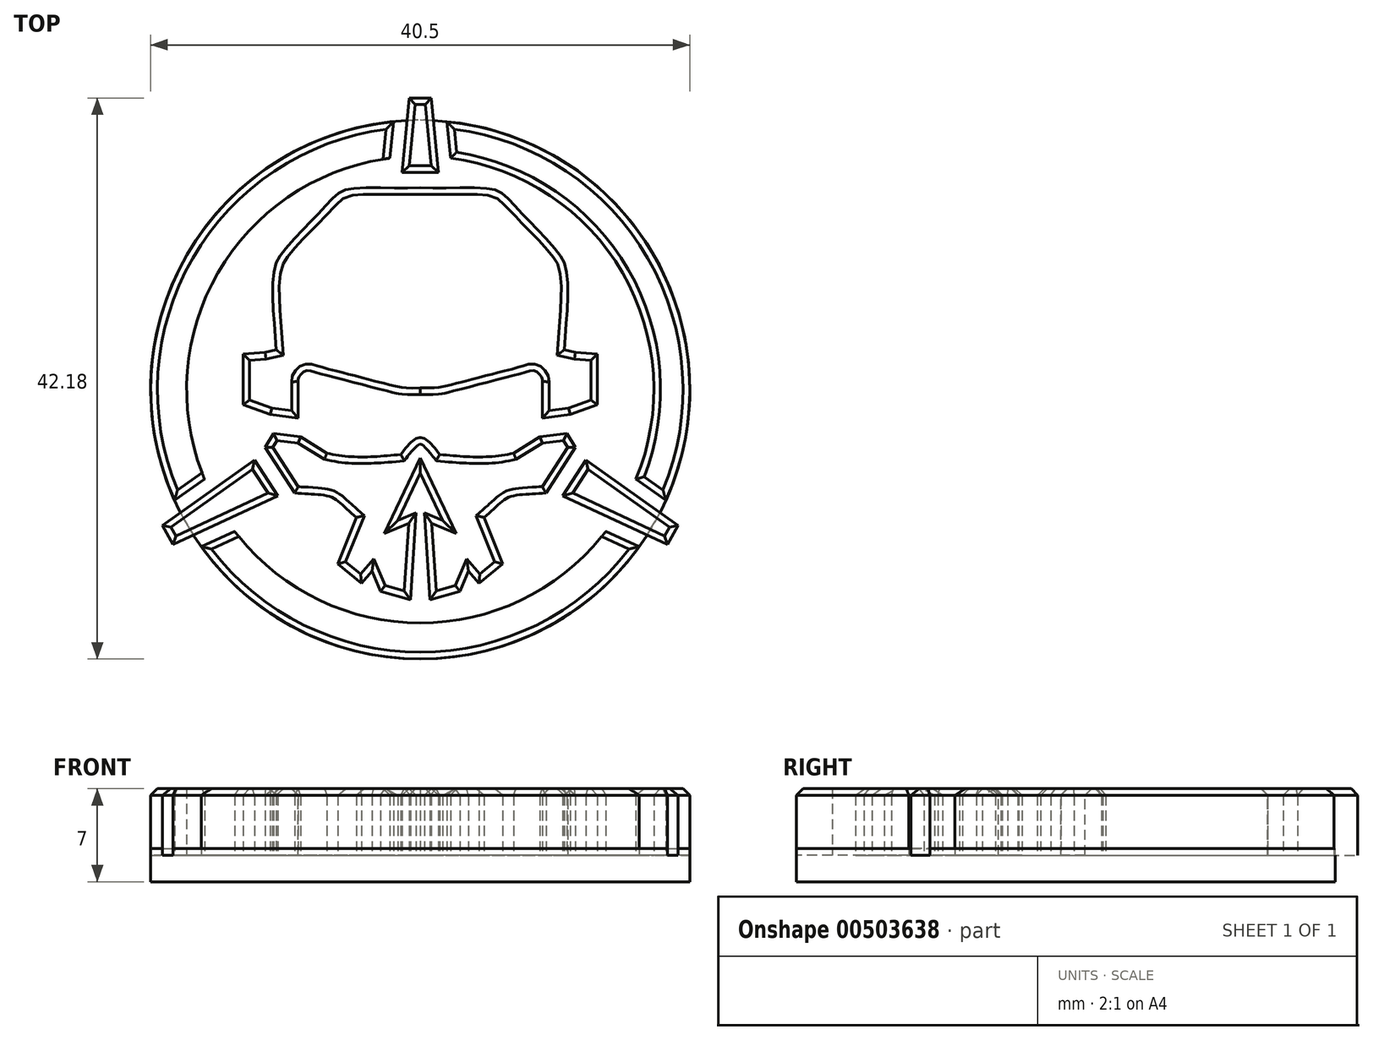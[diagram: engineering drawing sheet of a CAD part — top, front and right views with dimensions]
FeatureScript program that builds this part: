
annotation { "Feature Type Name" : "Feature", "Feature Type Description" : "" }
export const myFeature = defineFeature(function(context is Context, id is Id, definition is map)
    precondition{}
    {
        {
            var Q0;
            Q0=qCreatedBy(makeId("Top.planeOp"),FACE);
            var sketch = newSketch(context, id + "F0", { "sketchPlane" : qUnion([Q0])});
            skLineSegment(sketch, "E0", {"start": v(0, 16.33) * mm, "end": v(-1.37, 16.33) * mm});
            skLineSegment(sketch, "E1", {"start": v(-1.37, 16.33) * mm, "end": v(-0.83, 21.93) * mm});
            skLineSegment(sketch, "E2", {"start": v(-0.83, 21.93) * mm, "end": v(0, 21.93) * mm});
            skLineSegment(sketch, "E3.MirrorCS", {"start": v(1.37, 16.33) * mm, "end": v(0.83, 21.93) * mm});
            skLineSegment(sketch, "E4.MirrorCS", {"start": v(0.83, 21.93) * mm, "end": v(0, 21.93) * mm});
            skLineSegment(sketch, "E5.MirrorCS", {"start": v(0, 16.33) * mm, "end": v(1.37, 16.33) * mm});
            skLineSegment(sketch, "E6", {"start": v(-12.45, -5.3) * mm, "end": v(-10.71, -7.99) * mm});
            skLineSegment(sketch, "E7", {"start": v(-10.71, -7.99) * mm, "end": v(-18.58, -11.65) * mm});
            skLineSegment(sketch, "E8", {"start": v(-18.58, -11.65) * mm, "end": v(-19.38, -10.2) * mm});
            skLineSegment(sketch, "E9", {"start": v(-19.38, -10.2) * mm, "end": v(-12.45, -5.3) * mm});
            skLineSegment(sketch, "E10.MirrorCS", {"start": v(12.45, -5.3) * mm, "end": v(10.71, -7.99) * mm});
            skLineSegment(sketch, "E11.MirrorCS", {"start": v(18.58, -11.65) * mm, "end": v(19.38, -10.2) * mm});
            skLineSegment(sketch, "E12.MirrorCS", {"start": v(10.71, -7.99) * mm, "end": v(18.58, -11.65) * mm});
            skLineSegment(sketch, "E13.MirrorCS", {"start": v(19.38, -10.2) * mm, "end": v(12.45, -5.3) * mm});
            skSolve(sketch);
        }
        {
            var Q0;
            Q0=qCreatedBy(makeId("Top.planeOp"),FACE);
            var sketch = newSketch(context, id + "F1", { "sketchPlane" : qUnion([Q0])});
            skLineSegment(sketch, "E14", {"start": v(-11.02, -3.3) * mm, "end": v(-11.66, -4.36) * mm});
            skLineSegment(sketch, "E15", {"start": v(-11.66, -4.36) * mm, "end": v(-9.45, -7.78) * mm});
            skLineSegment(sketch, "E16", {"start": v(0, -6.29) * mm, "end": v(-1.7, -9.85) * mm});
            skLineSegment(sketch, "E17", {"start": v(-1.7, -9.85) * mm, "end": v(-0.31, -9.27) * mm});
            skLineSegment(sketch, "E18", {"start": v(-0.31, -9.27) * mm, "end": v(-0.74, -15.8) * mm});
            skLineSegment(sketch, "E19", {"start": v(-0.74, -15.8) * mm, "end": v(-2.99, -15.15) * mm});
            skLineSegment(sketch, "E20", {"start": v(-2.99, -15.15) * mm, "end": v(-3.63, -13.65) * mm});
            skLineSegment(sketch, "E21", {"start": v(-3.63, -13.65) * mm, "end": v(-4.4, -14.55) * mm});
            skLineSegment(sketch, "E22", {"start": v(-4.4, -14.55) * mm, "end": v(-6.2, -13.1) * mm});
            skLineSegment(sketch, "E23", {"start": v(-6.2, -13.1) * mm, "end": v(-4.8, -9.61) * mm});
            skLineSegment(sketch, "E24", {"start": v(-11.02, -3.3) * mm, "end": v(-9, -3.55) * mm});
            skLineSegment(sketch, "E25", {"start": v(-9, -3.55) * mm, "end": v(-7, -4.77) * mm});
            skFitSpline(sketch, "E26", {"points": [v(-7, -4.77) * mm, v(-4.43, -5.06) * mm, v(-1.46, -4.88) * mm], "startDerivative": vector(5.04, -1.32) * mm, "endDerivative": vector(5.85, 0.6) * mm});
            skLineSegment(sketch, "E27.MirrorCS", {"start": v(11.02, -3.3) * mm, "end": v(11.66, -4.36) * mm});
            skLineSegment(sketch, "E28.MirrorCS", {"start": v(11.66, -4.36) * mm, "end": v(9.45, -7.78) * mm});
            skLineSegment(sketch, "E29.MirrorCS", {"start": v(4.4, -14.55) * mm, "end": v(6.2, -13.1) * mm});
            skLineSegment(sketch, "E30.MirrorCS", {"start": v(3.63, -13.65) * mm, "end": v(4.4, -14.55) * mm});
            skLineSegment(sketch, "E31.MirrorCS", {"start": v(6.2, -13.1) * mm, "end": v(4.8, -9.61) * mm});
            skLineSegment(sketch, "E32.MirrorCS", {"start": v(2.99, -15.15) * mm, "end": v(3.63, -13.65) * mm});
            skLineSegment(sketch, "E33.MirrorCS", {"start": v(0.74, -15.8) * mm, "end": v(2.99, -15.15) * mm});
            skLineSegment(sketch, "E34.MirrorCS", {"start": v(11.02, -3.3) * mm, "end": v(9, -3.55) * mm});
            skLineSegment(sketch, "E35.MirrorCS", {"start": v(0.31, -9.27) * mm, "end": v(0.74, -15.8) * mm});
            skLineSegment(sketch, "E36.MirrorCS", {"start": v(0, -6.29) * mm, "end": v(1.7, -9.85) * mm});
            skFitSpline(sketch, "E37.MirrorCS", {"points": [v(7, -4.77) * mm, v(4.43, -5.06) * mm, v(1.46, -4.88) * mm], "startDerivative": vector(-5.04, -1.32) * mm, "endDerivative": vector(-5.85, 0.6) * mm});
            skLineSegment(sketch, "E38.MirrorCS", {"start": v(9, -3.55) * mm, "end": v(7, -4.77) * mm});
            skLineSegment(sketch, "E39.MirrorCS", {"start": v(1.7, -9.85) * mm, "end": v(0.31, -9.27) * mm});
            skFitSpline(sketch, "E40", {"points": [v(-1.46, -4.88) * mm, v(0, -3.6) * mm, v(1.46, -4.88) * mm], "startDerivative": vector(2.92, 3.83) * mm, "endDerivative": vector(2.92, -3.83) * mm});
            skFitSpline(sketch, "E41", {"points": [v(-9.45, -7.78) * mm, v(-8.13, -7.86) * mm, v(-7.03, -7.97) * mm, v(-6.32, -8.28) * mm, v(-5.68, -8.83) * mm, v(-4.8, -9.61) * mm], "startDerivative": vector(5.88, -0.42) * mm, "endDerivative": vector(4.32, -3.77) * mm});
            skFitSpline(sketch, "E42.MirrorCS", {"points": [v(9.45, -7.78) * mm, v(8.13, -7.86) * mm, v(7.03, -7.97) * mm, v(6.32, -8.28) * mm, v(5.68, -8.83) * mm, v(4.8, -9.61) * mm], "startDerivative": vector(-5.88, -0.42) * mm, "endDerivative": vector(-4.32, -3.77) * mm});
            skLineSegment(sketch, "E43", {"start": v(-9.17, -2.14) * mm, "end": v(-9.17, 0.6) * mm});
            skLineSegment(sketch, "E44", {"start": v(-9.17, -2.14) * mm, "end": v(-11.26, -1.88) * mm});
            skLineSegment(sketch, "E45", {"start": v(-11.26, -1.88) * mm, "end": v(-13.31, -1.13) * mm});
            skLineSegment(sketch, "E46", {"start": v(-13.31, -1.13) * mm, "end": v(-13.31, 2.68) * mm});
            skLineSegment(sketch, "E47", {"start": v(-13.31, 2.68) * mm, "end": v(-11.65, 2.79) * mm});
            skLineSegment(sketch, "E48", {"start": v(-11.65, 2.79) * mm, "end": v(-10.81, 2.98) * mm});
            skLineSegment(sketch, "E49.MirrorCS", {"start": v(9.17, -2.14) * mm, "end": v(9.17, 0.6) * mm});
            skLineSegment(sketch, "E50.MirrorCS", {"start": v(9.17, -2.14) * mm, "end": v(11.26, -1.88) * mm});
            skLineSegment(sketch, "E51.MirrorCS", {"start": v(13.31, 2.68) * mm, "end": v(11.65, 2.79) * mm});
            skLineSegment(sketch, "E52.MirrorCS", {"start": v(11.65, 2.79) * mm, "end": v(10.81, 2.98) * mm});
            skLineSegment(sketch, "E53.MirrorCS", {"start": v(13.31, -1.13) * mm, "end": v(13.31, 2.68) * mm});
            skLineSegment(sketch, "E54.MirrorCS", {"start": v(11.26, -1.88) * mm, "end": v(13.31, -1.13) * mm});
            skFitSpline(sketch, "E55", {"points": [v(-10.81, 2.98) * mm, v(-11, 5.49) * mm, v(-11.09, 8.03) * mm, v(-10.81, 9.53) * mm, v(-10.35, 10.34) * mm, v(-8.89, 11.95) * mm, v(-7.68, 13.2) * mm, v(-6.62, 14.32) * mm, v(-5.92, 14.9) * mm, v(-4.98, 15.14) * mm, v(-2.39, 15.17) * mm, v(0, 15.17) * mm], "startDerivative": vector(-1.63, 22.59) * mm, "endDerivative": vector(21.4, 0.1) * mm});
            skFitSpline(sketch, "E56", {"points": [v(-9.17, 0.6) * mm, v(-9.17, 0.76) * mm, v(-9.08, 0.98) * mm, v(-8.84, 1.28) * mm, v(-8.44, 1.44) * mm, v(-7.9, 1.32) * mm, v(-6.2, 0.86) * mm, v(-3.5, 0.16) * mm, v(-1.98, -0.23) * mm, v(-1.7, -0.3) * mm, v(-1.26, -0.36) * mm, v(0, -0.37) * mm], "startDerivative": vector(-0.28, 2.53) * mm, "endDerivative": vector(9.94, 0.33) * mm});
            skFitSpline(sketch, "E57.MirrorCS", {"points": [v(9.17, 0.6) * mm, v(9.17, 0.76) * mm, v(9.08, 0.98) * mm, v(8.84, 1.28) * mm, v(8.44, 1.44) * mm, v(7.9, 1.32) * mm, v(6.2, 0.86) * mm, v(3.5, 0.16) * mm, v(1.98, -0.23) * mm, v(1.7, -0.3) * mm, v(1.26, -0.36) * mm, v(0, -0.37) * mm], "startDerivative": vector(0.28, 2.53) * mm, "endDerivative": vector(-9.94, 0.33) * mm});
            skFitSpline(sketch, "E58.MirrorCS", {"points": [v(10.81, 2.98) * mm, v(11, 5.49) * mm, v(11.09, 8.03) * mm, v(10.81, 9.53) * mm, v(10.35, 10.34) * mm, v(8.89, 11.95) * mm, v(7.68, 13.2) * mm, v(6.62, 14.32) * mm, v(5.92, 14.9) * mm, v(4.98, 15.14) * mm, v(2.39, 15.17) * mm, v(0, 15.17) * mm], "startDerivative": vector(1.63, 22.59) * mm, "endDerivative": vector(-21.4, 0.1) * mm});
            skSolve(sketch);
        }
        {
            var Q0;
            Q0=qCreatedBy(makeId("Top.planeOp"),FACE);
            var sketch = newSketch(context, id + "F2", { "sketchPlane" : qUnion([Q0])});
            skLineSegment(sketch, "E59.0", {"start": v(-2.27, 17.4) * mm, "end": v(-2, 20.14) * mm});
            skLineSegment(sketch, "E60.MirrorCS", {"start": v(2.27, 17.4) * mm, "end": v(2, 20.14) * mm});
            skLineSegment(sketch, "E61.0", {"start": v(-18.45, -8.32) * mm, "end": v(-16.2, -6.73) * mm});
            skLineSegment(sketch, "E62.MirrorCS", {"start": v(-16.46, -11.8) * mm, "end": v(-13.95, -10.65) * mm});
            skArc(sketch, "E63", {"start": v(-2, 20.14) * mm, "mid": v(-17.53, 10.13) * mm, "end": v(-18.45, -8.32) * mm});
            skArc(sketch, "E64", {"start": v(-2.27, 17.4) * mm, "mid": v(-15.2, 8.78) * mm, "end": v(-16.2, -6.73) * mm});
            skPoint(sketch, "E65.orphan", {"position": v(-1.82, 22.03) * mm});
            skPoint(sketch, "E66.orphan", {"position": v(1.82, 22.03) * mm});
            skPoint(sketch, "E67.orphan", {"position": v(-2.4, 16.07) * mm});
            skPoint(sketch, "E68.orphan", {"position": v(2.4, 16.07) * mm});
            skPoint(sketch, "E69.orphan", {"position": v(-19.96, -9.39) * mm});
            skPoint(sketch, "E70.orphan", {"position": v(-18.13, -12.56) * mm});
            skArc(sketch, "E71.trimOffspring", {"start": v(-16.46, -11.8) * mm, "mid": v(0, -20.24) * mm, "end": v(16.46, -11.8) * mm});
            skArc(sketch, "E72.trimOffspring", {"start": v(-13.95, -10.65) * mm, "mid": v(0, -17.55) * mm, "end": v(13.95, -10.65) * mm});
            skPoint(sketch, "E73.orphan", {"position": v(-10.42, -9.03) * mm});
            skPoint(sketch, "E74.orphan", {"position": v(-13.03, -4.48) * mm});
            skLineSegment(sketch, "E75.MirrorCS", {"start": v(18.45, -8.32) * mm, "end": v(16.2, -6.73) * mm});
            skLineSegment(sketch, "E76.MirrorCS", {"start": v(16.46, -11.8) * mm, "end": v(13.95, -10.65) * mm});
            skArc(sketch, "E77.MirrorCS", {"start": v(13.95, -10.65) * mm, "mid": v(0, -17.55) * mm, "end": v(-13.95, -10.65) * mm});
            skArc(sketch, "E78.trimOffspring", {"start": v(16.2, -6.73) * mm, "mid": v(15.2, 8.78) * mm, "end": v(2.27, 17.4) * mm});
            skArc(sketch, "E79.trimOffspring", {"start": v(18.45, -8.32) * mm, "mid": v(17.53, 10.13) * mm, "end": v(2, 20.14) * mm});
            skArc(sketch, "E80.trimOffspring", {"start": v(-16.2, -6.73) * mm, "mid": v(-15.2, 8.78) * mm, "end": v(-2.27, 17.4) * mm});
            skSolve(sketch);
        }
        {
            var Q0;
            Q0=makeQuery(id+"F1.imprint","IMPRINT",FACE,{"disambiguationData":[TD([[makeQuery(id+"F1.imprint","IMPRINT",EDGE,{"derivedFrom":sQuery(id+"F1.wireOp",EDGE,"E14")}),1.0]])]});
            var Q1;
            Q1=makeQuery(id+"F0.imprint","IMPRINT",FACE,{"disambiguationData":[TD([[makeQuery(id+"F0.imprint","IMPRINT",EDGE,{"derivedFrom":sQuery(id+"F0.wireOp",EDGE,"E0")}),-1.0]])]});
            var Q2;
            Q2=makeQuery(id+"F1.imprint","IMPRINT",FACE,{"disambiguationData":[TD([[makeQuery(id+"F1.imprint","IMPRINT",EDGE,{"derivedFrom":sQuery(id+"F1.wireOp",EDGE,"E43")}),1.0]])]});
            var Q3;
            Q3=makeQuery(id+"F2.imprint","IMPRINT",FACE,{"disambiguationData":[TD([[makeQuery(id+"F2.imprint","IMPRINT",EDGE,{"derivedFrom":sQuery(id+"F2.wireOp",EDGE,"E60.MirrorCS")}),-1.0]])]});
            var Q4;
            Q4=makeQuery(id+"F0.imprint","IMPRINT",FACE,{"disambiguationData":[TD([[makeQuery(id+"F0.imprint","IMPRINT",EDGE,{"derivedFrom":sQuery(id+"F0.wireOp",EDGE,"E10.MirrorCS")}),1.0]])]});
            var Q5;
            Q5=makeQuery(id+"F2.imprint","IMPRINT",FACE,{"disambiguationData":[TD([[makeQuery(id+"F2.imprint","IMPRINT",EDGE,{"derivedFrom":sQuery(id+"F2.wireOp",EDGE,"E62.MirrorCS")}),-1.0]])]});
            var Q6;
            Q6=makeQuery(id+"F2.imprint","IMPRINT",FACE,{"disambiguationData":[TD([[makeQuery(id+"F2.imprint","IMPRINT",EDGE,{"derivedFrom":sQuery(id+"F2.wireOp",EDGE,"E59.0")}),1.0]])]});
            var Q7;
            Q7=makeQuery(id+"F0.imprint","IMPRINT",FACE,{"disambiguationData":[TD([[makeQuery(id+"F0.imprint","IMPRINT",EDGE,{"derivedFrom":sQuery(id+"F0.wireOp",EDGE,"E6")}),-1.0]])]});
            extrude(context, id + "F3", {"entities" : qUnion([Q0, Q1, Q2, Q3, Q4, Q5, Q6, Q7]), "depth" : 5 * mm});
        }
        {
            var Q0;
            Q0=makeQuery(id+"F3.opExtrude","CAP_EDGE",EDGE,{"disambiguationData":[OSD([sQuery(id+"F2.wireOp",EDGE,"E80.trimOffspring")])],"isStart":false});
            var Q1;
            Q1=makeQuery(id+"F3.opExtrude","CAP_EDGE",EDGE,{"disambiguationData":[OSD([sQuery(id+"F0.wireOp",EDGE,"E11.MirrorCS")])],"isStart":false});
            var Q2;
            Q2=makeQuery(id+"F3.opExtrude","CAP_EDGE",EDGE,{"disambiguationData":[OSD([sQuery(id+"F0.wireOp",EDGE,"E8")])],"isStart":false});
            var Q3;
            Q3=makeQuery(id+"F3.opExtrude","CAP_EDGE",EDGE,{"disambiguationData":[OSD([sQuery(id+"F2.wireOp",EDGE,"E79.trimOffspring")])],"isStart":false});
            var Q4;
            Q4=makeQuery(id+"F3.opExtrude","CAP_EDGE",EDGE,{"disambiguationData":[OSD([sQuery(id+"F2.wireOp",EDGE,"E78.trimOffspring")])],"isStart":false});
            var Q5;
            Q5=makeQuery(id+"F3.opExtrude","CAP_EDGE",EDGE,{"disambiguationData":[OSD([sQuery(id+"F2.wireOp",EDGE,"E71.trimOffspring")])],"isStart":false});
            var Q6;
            Q6=makeQuery(id+"F3.opExtrude","CAP_EDGE",EDGE,{"disambiguationData":[OSD([sQuery(id+"F2.wireOp",EDGE,"E77.MirrorCS")])],"isStart":false});
            var Q7;
            Q7=makeQuery(id+"F3.opExtrude","CAP_EDGE",EDGE,{"disambiguationData":[OSD([sQuery(id+"F1.wireOp",EDGE,"E45")])],"isStart":false});
            var Q8;
            Q8=makeQuery(id+"F3.opExtrude","CAP_EDGE",EDGE,{"disambiguationData":[OSD([sQuery(id+"F1.wireOp",EDGE,"E58.MirrorCS")])],"isStart":false});
            var Q9;
            Q9=makeQuery(id+"F3.opExtrude","CAP_EDGE",EDGE,{"disambiguationData":[OSD([sQuery(id+"F2.wireOp",EDGE,"E63")])],"isStart":false});
            var Q10;
            Q10=makeQuery(id+"F3.opExtrude","CAP_EDGE",EDGE,{"disambiguationData":[OSD([sQuery(id+"F0.wireOp",EDGE,"E10.MirrorCS")])],"isStart":false});
            var Q11;
            Q11=makeQuery(id+"F3.opExtrude","CAP_EDGE",EDGE,{"disambiguationData":[OSD([sQuery(id+"F0.wireOp",EDGE,"E13.MirrorCS")])],"isStart":false});
            var Q12;
            Q12=makeQuery(id+"F3.opExtrude","CAP_EDGE",EDGE,{"disambiguationData":[OSD([sQuery(id+"F0.wireOp",EDGE,"E12.MirrorCS")])],"isStart":false});
            var Q13;
            Q13=makeQuery(id+"F3.opExtrude","CAP_EDGE",EDGE,{"disambiguationData":[OSD([sQuery(id+"F0.wireOp",EDGE,"E7")])],"isStart":false});
            var Q14;
            Q14=makeQuery(id+"F3.opExtrude","CAP_EDGE",EDGE,{"disambiguationData":[OSD([sQuery(id+"F0.wireOp",EDGE,"E6")])],"isStart":false});
            var Q15;
            Q15=makeQuery(id+"F3.opExtrude","CAP_EDGE",EDGE,{"disambiguationData":[OSD([sQuery(id+"F0.wireOp",EDGE,"E9")])],"isStart":false});
            var Q16;
            Q16=makeQuery(id+"F3.opExtrude","CAP_EDGE",EDGE,{"disambiguationData":[OSD([sQuery(id+"F1.wireOp",EDGE,"E42.MirrorCS")])],"isStart":false});
            var Q17;
            Q17=makeQuery(id+"F3.opExtrude","CAP_EDGE",EDGE,{"disambiguationData":[OSD([sQuery(id+"F1.wireOp",EDGE,"E15")])],"isStart":false});
            var Q18;
            Q18=makeQuery(id+"F3.opExtrude","CAP_EDGE",EDGE,{"disambiguationData":[OSD([sQuery(id+"F1.wireOp",EDGE,"E22")])],"isStart":false});
            var Q19;
            Q19=makeQuery(id+"F3.opExtrude","CAP_EDGE",EDGE,{"disambiguationData":[OSD([sQuery(id+"F1.wireOp",EDGE,"E19")])],"isStart":false});
            var Q20;
            Q20=makeQuery(id+"F3.opExtrude","CAP_EDGE",EDGE,{"disambiguationData":[OSD([sQuery(id+"F1.wireOp",EDGE,"E41")])],"isStart":false});
            var Q21;
            Q21=makeQuery(id+"F3.opExtrude","CAP_EDGE",EDGE,{"disambiguationData":[OSD([sQuery(id+"F1.wireOp",EDGE,"E32.MirrorCS")])],"isStart":false});
            var Q22;
            Q22=makeQuery(id+"F3.opExtrude","CAP_EDGE",EDGE,{"disambiguationData":[OSD([sQuery(id+"F1.wireOp",EDGE,"E16")])],"isStart":false});
            var Q23;
            Q23=makeQuery(id+"F3.opExtrude","CAP_EDGE",EDGE,{"disambiguationData":[OSD([sQuery(id+"F1.wireOp",EDGE,"E28.MirrorCS")])],"isStart":false});
            var Q24;
            Q24=makeQuery(id+"F3.opExtrude","CAP_EDGE",EDGE,{"disambiguationData":[OSD([sQuery(id+"F2.wireOp",EDGE,"E60.MirrorCS")])],"isStart":false});
            var Q25;
            Q25=makeQuery(id+"F3.opExtrude","CAP_EDGE",EDGE,{"disambiguationData":[OSD([sQuery(id+"F2.wireOp",EDGE,"E76.MirrorCS")])],"isStart":false});
            var Q26;
            Q26=makeQuery(id+"F3.opExtrude","CAP_EDGE",EDGE,{"disambiguationData":[OSD([sQuery(id+"F2.wireOp",EDGE,"E62.MirrorCS")])],"isStart":false});
            var Q27;
            Q27=makeQuery(id+"F3.opExtrude","CAP_EDGE",EDGE,{"disambiguationData":[OSD([sQuery(id+"F1.wireOp",EDGE,"E55")])],"isStart":false});
            var Q28;
            Q28=makeQuery(id+"F3.opExtrude","CAP_EDGE",EDGE,{"disambiguationData":[OSD([sQuery(id+"F1.wireOp",EDGE,"E46")])],"isStart":false});
            var Q29;
            Q29=makeQuery(id+"F3.opExtrude","CAP_EDGE",EDGE,{"disambiguationData":[OSD([sQuery(id+"F1.wireOp",EDGE,"E48")])],"isStart":false});
            var Q30;
            Q30=makeQuery(id+"F3.opExtrude","CAP_EDGE",EDGE,{"disambiguationData":[OSD([sQuery(id+"F1.wireOp",EDGE,"E56")])],"isStart":false});
            var Q31;
            Q31=makeQuery(id+"F3.opExtrude","CAP_EDGE",EDGE,{"disambiguationData":[OSD([sQuery(id+"F1.wireOp",EDGE,"E47")])],"isStart":false});
            var Q32;
            Q32=makeQuery(id+"F3.opExtrude","CAP_EDGE",EDGE,{"disambiguationData":[OSD([sQuery(id+"F2.wireOp",EDGE,"E61.0")])],"isStart":false});
            var Q33;
            Q33=makeQuery(id+"F3.opExtrude","CAP_EDGE",EDGE,{"disambiguationData":[OSD([sQuery(id+"F2.wireOp",EDGE,"E59.0")])],"isStart":false});
            var Q34;
            Q34=makeQuery(id+"F3.opExtrude","CAP_EDGE",EDGE,{"disambiguationData":[OSD([sQuery(id+"F0.wireOp",EDGE,"E0"),sQuery(id+"F0.wireOp",EDGE,"E5.MirrorCS")])],"isStart":false});
            var Q35;
            Q35=makeQuery(id+"F3.opExtrude","CAP_EDGE",EDGE,{"disambiguationData":[OSD([sQuery(id+"F1.wireOp",EDGE,"E30.MirrorCS")])],"isStart":false});
            var Q36;
            Q36=makeQuery(id+"F3.opExtrude","CAP_EDGE",EDGE,{"disambiguationData":[OSD([sQuery(id+"F1.wireOp",EDGE,"E39.MirrorCS")])],"isStart":false});
            var Q37;
            Q37=makeQuery(id+"F3.opExtrude","CAP_EDGE",EDGE,{"disambiguationData":[OSD([sQuery(id+"F1.wireOp",EDGE,"E29.MirrorCS")])],"isStart":false});
            var Q38;
            Q38=makeQuery(id+"F3.opExtrude","CAP_EDGE",EDGE,{"disambiguationData":[OSD([sQuery(id+"F1.wireOp",EDGE,"E24")])],"isStart":false});
            var Q39;
            Q39=makeQuery(id+"F3.opExtrude","CAP_EDGE",EDGE,{"disambiguationData":[OSD([sQuery(id+"F1.wireOp",EDGE,"E35.MirrorCS")])],"isStart":false});
            var Q40;
            Q40=makeQuery(id+"F3.opExtrude","CAP_EDGE",EDGE,{"disambiguationData":[OSD([sQuery(id+"F1.wireOp",EDGE,"E20")])],"isStart":false});
            var Q41;
            Q41=makeQuery(id+"F3.opExtrude","CAP_EDGE",EDGE,{"disambiguationData":[OSD([sQuery(id+"F1.wireOp",EDGE,"E27.MirrorCS")])],"isStart":false});
            var Q42;
            Q42=makeQuery(id+"F3.opExtrude","CAP_EDGE",EDGE,{"disambiguationData":[OSD([sQuery(id+"F1.wireOp",EDGE,"E34.MirrorCS")])],"isStart":false});
            var Q43;
            Q43=makeQuery(id+"F3.opExtrude","CAP_EDGE",EDGE,{"disambiguationData":[OSD([sQuery(id+"F1.wireOp",EDGE,"E25")])],"isStart":false});
            var Q44;
            Q44=makeQuery(id+"F3.opExtrude","CAP_EDGE",EDGE,{"disambiguationData":[OSD([sQuery(id+"F1.wireOp",EDGE,"E18")])],"isStart":false});
            var Q45;
            Q45=makeQuery(id+"F3.opExtrude","CAP_EDGE",EDGE,{"disambiguationData":[OSD([sQuery(id+"F1.wireOp",EDGE,"E36.MirrorCS")])],"isStart":false});
            var Q46;
            Q46=makeQuery(id+"F3.opExtrude","CAP_EDGE",EDGE,{"disambiguationData":[OSD([sQuery(id+"F1.wireOp",EDGE,"E26")])],"isStart":false});
            var Q47;
            Q47=makeQuery(id+"F3.opExtrude","CAP_EDGE",EDGE,{"disambiguationData":[OSD([sQuery(id+"F1.wireOp",EDGE,"E14")])],"isStart":false});
            var Q48;
            Q48=makeQuery(id+"F3.opExtrude","CAP_EDGE",EDGE,{"disambiguationData":[OSD([sQuery(id+"F1.wireOp",EDGE,"E38.MirrorCS")])],"isStart":false});
            var Q49;
            Q49=makeQuery(id+"F3.opExtrude","CAP_EDGE",EDGE,{"disambiguationData":[OSD([sQuery(id+"F1.wireOp",EDGE,"E40")])],"isStart":false});
            var Q50;
            Q50=makeQuery(id+"F3.opExtrude","CAP_EDGE",EDGE,{"disambiguationData":[OSD([sQuery(id+"F1.wireOp",EDGE,"E33.MirrorCS")])],"isStart":false});
            var Q51;
            Q51=makeQuery(id+"F3.opExtrude","CAP_EDGE",EDGE,{"disambiguationData":[OSD([sQuery(id+"F1.wireOp",EDGE,"E21")])],"isStart":false});
            var Q52;
            Q52=makeQuery(id+"F3.opExtrude","CAP_EDGE",EDGE,{"disambiguationData":[OSD([sQuery(id+"F1.wireOp",EDGE,"E37.MirrorCS")])],"isStart":false});
            var Q53;
            Q53=makeQuery(id+"F3.opExtrude","CAP_EDGE",EDGE,{"disambiguationData":[OSD([sQuery(id+"F1.wireOp",EDGE,"E17")])],"isStart":false});
            var Q54;
            Q54=makeQuery(id+"F3.opExtrude","CAP_EDGE",EDGE,{"disambiguationData":[OSD([sQuery(id+"F1.wireOp",EDGE,"E23")])],"isStart":false});
            var Q55;
            Q55=makeQuery(id+"F3.opExtrude","CAP_EDGE",EDGE,{"disambiguationData":[OSD([sQuery(id+"F2.wireOp",EDGE,"E75.MirrorCS")])],"isStart":false});
            var Q56;
            Q56=makeQuery(id+"F3.opExtrude","CAP_EDGE",EDGE,{"disambiguationData":[OSD([sQuery(id+"F1.wireOp",EDGE,"E54.MirrorCS")])],"isStart":false});
            var Q57;
            Q57=makeQuery(id+"F3.opExtrude","CAP_EDGE",EDGE,{"disambiguationData":[OSD([sQuery(id+"F1.wireOp",EDGE,"E53.MirrorCS")])],"isStart":false});
            var Q58;
            Q58=makeQuery(id+"F3.opExtrude","CAP_EDGE",EDGE,{"disambiguationData":[OSD([sQuery(id+"F1.wireOp",EDGE,"E43")])],"isStart":false});
            var Q59;
            Q59=makeQuery(id+"F3.opExtrude","CAP_EDGE",EDGE,{"disambiguationData":[OSD([sQuery(id+"F0.wireOp",EDGE,"E3.MirrorCS")])],"isStart":false});
            var Q60;
            Q60=makeQuery(id+"F3.opExtrude","CAP_EDGE",EDGE,{"disambiguationData":[OSD([sQuery(id+"F0.wireOp",EDGE,"E1")])],"isStart":false});
            var Q61;
            Q61=makeQuery(id+"F3.opExtrude","CAP_EDGE",EDGE,{"disambiguationData":[OSD([sQuery(id+"F0.wireOp",EDGE,"E2"),sQuery(id+"F0.wireOp",EDGE,"E4.MirrorCS")])],"isStart":false});
            var Q62;
            Q62=makeQuery(id+"F3.opExtrude","CAP_EDGE",EDGE,{"disambiguationData":[OSD([sQuery(id+"F1.wireOp",EDGE,"E31.MirrorCS")])],"isStart":false});
            var Q63;
            Q63=makeQuery(id+"F3.opExtrude","CAP_EDGE",EDGE,{"disambiguationData":[OSD([sQuery(id+"F1.wireOp",EDGE,"E51.MirrorCS")])],"isStart":false});
            var Q64;
            Q64=makeQuery(id+"F3.opExtrude","CAP_EDGE",EDGE,{"disambiguationData":[OSD([sQuery(id+"F1.wireOp",EDGE,"E52.MirrorCS")])],"isStart":false});
            var Q65;
            Q65=makeQuery(id+"F3.opExtrude","CAP_EDGE",EDGE,{"disambiguationData":[OSD([sQuery(id+"F1.wireOp",EDGE,"E44")])],"isStart":false});
            var Q66;
            Q66=makeQuery(id+"F3.opExtrude","CAP_EDGE",EDGE,{"disambiguationData":[OSD([sQuery(id+"F1.wireOp",EDGE,"E50.MirrorCS")])],"isStart":false});
            var Q67;
            Q67=makeQuery(id+"F3.opExtrude","CAP_EDGE",EDGE,{"disambiguationData":[OSD([sQuery(id+"F1.wireOp",EDGE,"E57.MirrorCS")])],"isStart":false});
            var Q68;
            Q68=makeQuery(id+"F3.opExtrude","CAP_EDGE",EDGE,{"disambiguationData":[OSD([sQuery(id+"F1.wireOp",EDGE,"E49.MirrorCS")])],"isStart":false});
            chamfer(context, id + "F4", {"entities" : qUnion([Q0, Q1, Q2, Q3, Q4, Q5, Q6, Q7, Q8, Q9, Q10, Q11, Q12, Q13, Q14, Q15, Q16, Q17, Q18, Q19, Q20, Q21, Q22, Q23, Q24, Q25, Q26, Q27, Q28, Q29, Q30, Q31, Q32, Q33, Q34, Q35, Q36, Q37, Q38, Q39, Q40, Q41, Q42, Q43, Q44, Q45, Q46, Q47, Q48, Q49, Q50, Q51, Q52, Q53, Q54, Q55, Q56, Q57, Q58, Q59, Q60, Q61, Q62, Q63, Q64, Q65, Q66, Q67, Q68]), "width" : .5 * mm, "tangentPropagation" : true});
        }
        {
            var Q0;
            Q0=qCreatedBy(makeId("Top.planeOp"),FACE);
            var sketch = newSketch(context, id + "F5", { "sketchPlane" : qUnion([Q0])});
            skCircle(sketch, "E81", {"center": v(0, 0) * mm, "radius": 20.25 * mm});
            skSolve(sketch);
        }
        {
            var Q0;
            Q0=makeQuery(id+"F5.imprint","IMPRINT",FACE,{"disambiguationData":[TD([[makeQuery(id+"F5.imprint","IMPRINT",EDGE,{"derivedFrom":sQuery(id+"F5.wireOp",EDGE,"E81")}),1.0]])]});
            extrude(context, id + "F6", {"entities" : qUnion([Q0]), "oppositeDirection" : true, "depth" : 2 * mm, "hasSecondDirection" : true, "secondDirectionOppositeDirection" : false, "secondDirectionDepth" : .5 * mm});
        }
    });
